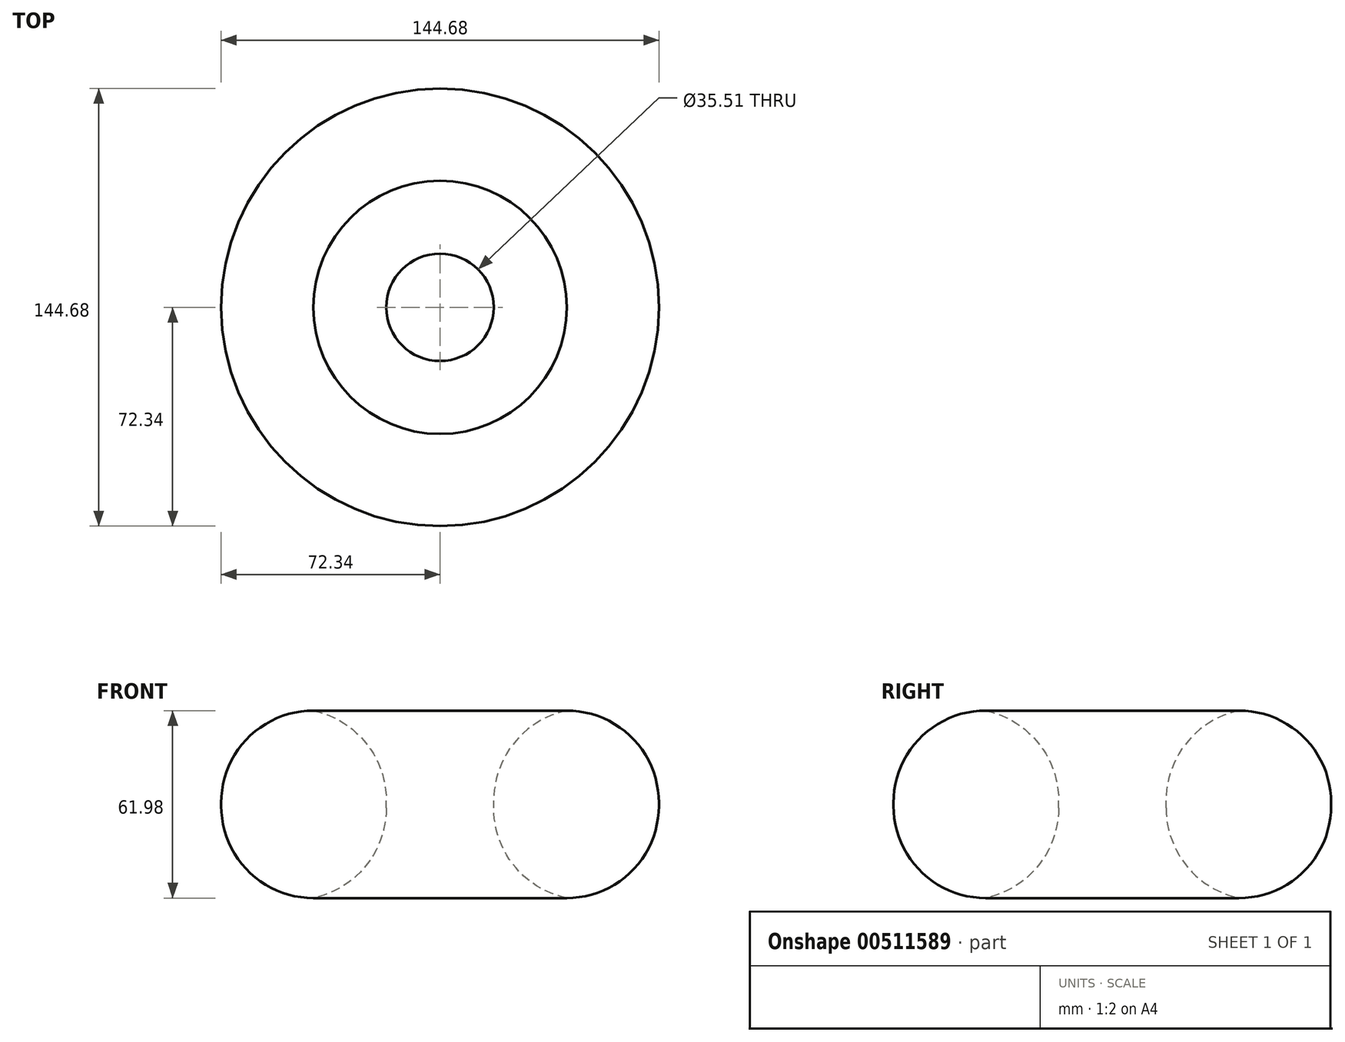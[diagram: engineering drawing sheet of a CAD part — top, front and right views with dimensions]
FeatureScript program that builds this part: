
annotation { "Feature Type Name" : "Feature", "Feature Type Description" : "" }
export const myFeature = defineFeature(function(context is Context, id is Id, definition is map)
    precondition{}
    {
        {
            var Q0;
            Q0=qCreatedBy(makeId("Top.planeOp"),FACE);
            var sketch = newSketch(context, id + "F0", { "sketchPlane" : qUnion([Q0])});
            skCircle(sketch, "E0", {"center": v(0, 0) * mm, "radius": 72.34 * mm});
            skSolve(sketch);
        }
        {
            var Q0;
            Q0=makeQuery(id+"F0.imprint","IMPRINT",FACE,{"disambiguationData":[TD([[makeQuery(id+"F0.imprint","IMPRINT",EDGE,{"derivedFrom":sQuery(id+"F0.wireOp",EDGE,"E0")}),1.0]])]});
            extrude(context, id + "F1", {"entities" : qUnion([Q0]), "depth" : 61.98 * mm, "offsetDistance" : 25.4 * mm});
        }
        {
            var Q0;
            Q0=makeQuery(id+"F1.opExtrude","CAP_FACE",FACE,{"disambiguationData":[OSD([sQuery(id+"F0.wireOp",EDGE,"E0")])],"isStart":false});
            var sketch = newSketch(context, id + "F2", { "sketchPlane" : qUnion([Q0])});
            skCircle(sketch, "E1", {"center": v(0, 0) * mm, "radius": 17.76 * mm});
            skSolve(sketch);
        }
        {
            var Q0;
            Q0=makeQuery(id+"F2.imprint","IMPRINT",FACE,{"disambiguationData":[TD([[makeQuery(id+"F2.imprint","IMPRINT",EDGE,{"derivedFrom":sQuery(id+"F2.wireOp",EDGE,"E1")}),1.0]])]});
            extrude(context, id + "F3", {"entities" : qUnion([Q0]), "operationType" : NewBodyOperationType.REMOVE, "oppositeDirection" : true, "depth" : 66.94 * mm, "offsetDistance" : 25.4 * mm});
        }
        {
            var Q0;
            Q0=makeQuery(id+"F1.opExtrude","CAP_EDGE",EDGE,{"disambiguationData":[OSD([sQuery(id+"F0.wireOp",EDGE,"E0")])],"isStart":false});
            var Q1;
            Q1=makeQuery(id+"F1.opExtrude","SWEPT_FACE",FACE,{"disambiguationData":[OSD([sQuery(id+"F0.wireOp",EDGE,"E0")])]});
            fillet(context, id + "F4", {"entities" : qUnion([Q0, Q1]), "radius" : 30.48 * mm, "tangentPropagation" : true, "allowEdgeOverflow" : false});
        }
        {
            var Q0;
            Q0=makeQuery(id+"F3.boolean.opBoolean","COPY",FACE,{"derivedFrom":makeQuery(id+"F3.opExtrude","SWEPT_FACE",FACE,{"disambiguationData":[OSD([sQuery(id+"F2.wireOp",EDGE,"E1")])]})});
            fillet(context, id + "F5", {"entities" : qUnion([Q0]), "radius" : 30.48 * mm, "tangentPropagation" : true, "allowEdgeOverflow" : false});
        }
    });
